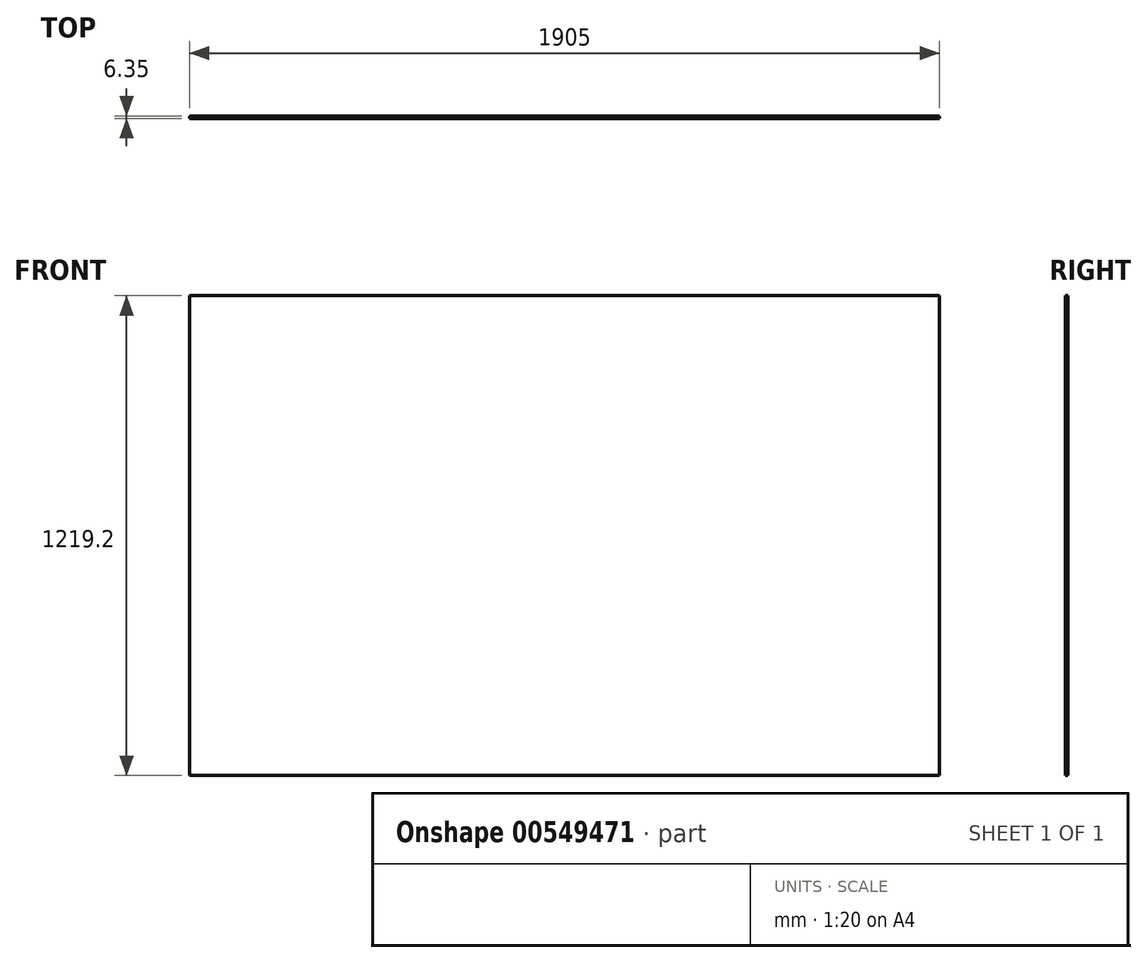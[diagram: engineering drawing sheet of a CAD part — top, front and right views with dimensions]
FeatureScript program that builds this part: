
annotation { "Feature Type Name" : "Feature", "Feature Type Description" : "" }
export const myFeature = defineFeature(function(context is Context, id is Id, definition is map)
    precondition{}
    {
        {
            var Q0;
            Q0=qCreatedBy(makeId("Front.planeOp"),FACE);
            var sketch = newSketch(context, id + "F0", { "sketchPlane" : qUnion([Q0])});
            skLineSegment(sketch, "E0.bottom", {"start": v(-952.5, 609.6) * mm, "end": v(952.5, 609.6) * mm});
            skLineSegment(sketch, "E0.top", {"start": v(-952.5, -609.6) * mm, "end": v(952.5, -609.6) * mm});
            skLineSegment(sketch, "E0.left", {"start": v(-952.5, 609.6) * mm, "end": v(-952.5, -609.6) * mm});
            skLineSegment(sketch, "E0.right", {"start": v(952.5, 609.6) * mm, "end": v(952.5, -609.6) * mm});
            skPoint(sketch, "E0.middle", {"position": v(0, 0) * mm});
            skSolve(sketch);
        }
        {
            var Q0;
            Q0 = qSketchRegion(id + "F0", true);
            extrude(context, id + "F1", {"entities" : qUnion([Q0]), "depth" : 6.35 * mm, "offsetDistance" : 25.4 * mm});
        }
    });
